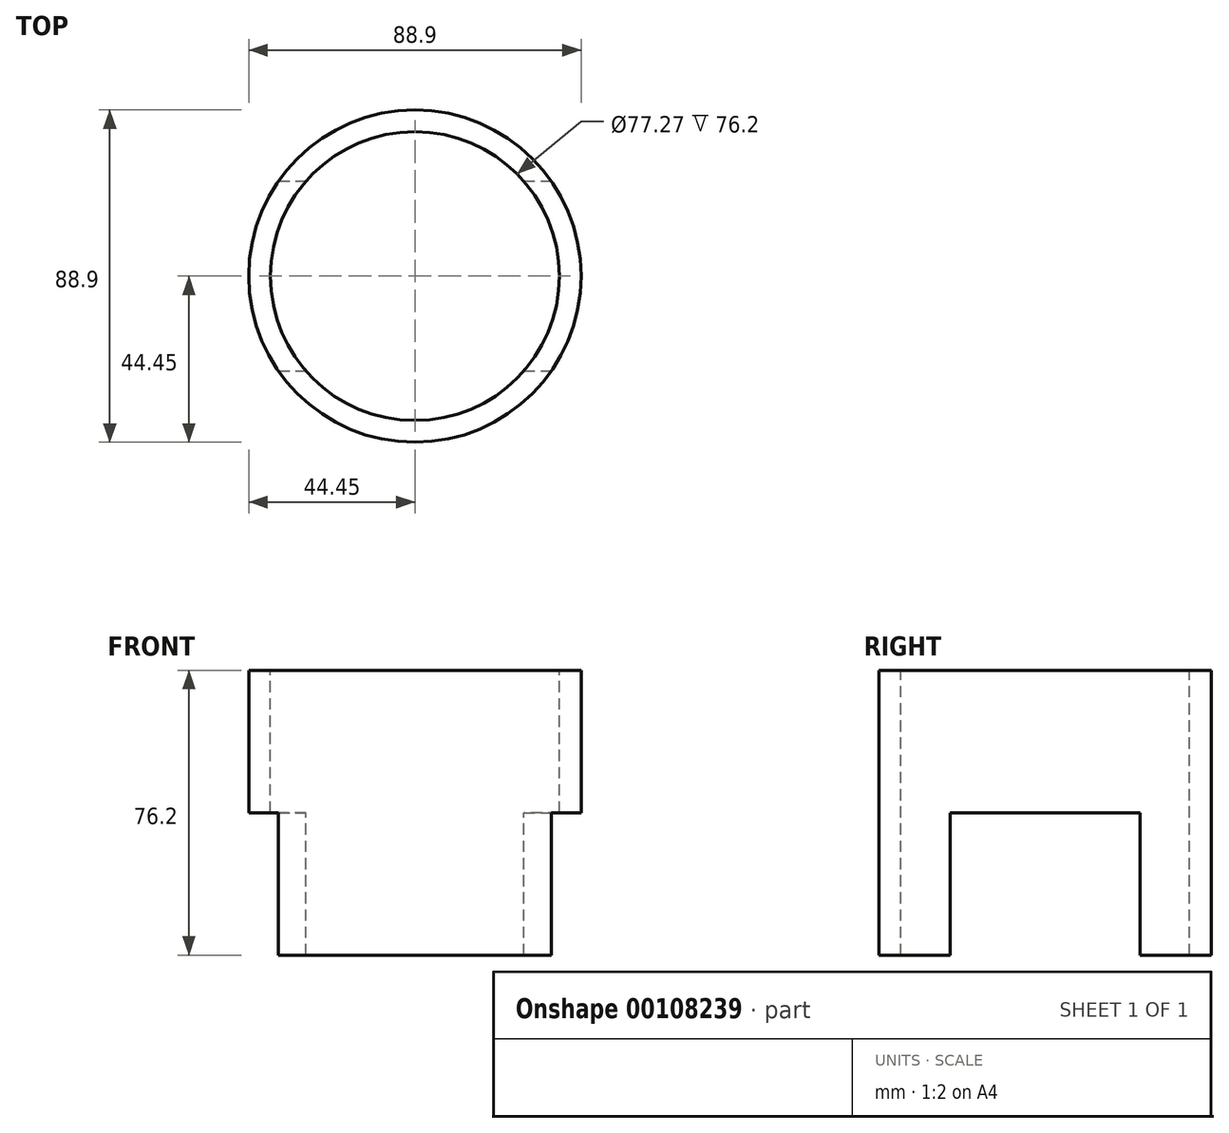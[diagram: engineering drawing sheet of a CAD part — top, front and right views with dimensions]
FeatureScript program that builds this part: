
annotation { "Feature Type Name" : "Feature", "Feature Type Description" : "" }
export const myFeature = defineFeature(function(context is Context, id is Id, definition is map)
    precondition{}
    {
        {
            var Q0;
            Q0=qCreatedBy(makeId("Front.planeOp"),FACE);
            var sketch = newSketch(context, id + "F0", { "sketchPlane" : qUnion([Q0])});
            skLineSegment(sketch, "E0", {"start": v(0, 190.5) * mm, "end": v(0, -190.5) * mm, "construction": true});
            skLineSegment(sketch, "E1", {"start": v(38.63, -38.1) * mm, "end": v(38.63, 38.1) * mm});
            skLineSegment(sketch, "E2", {"start": v(44.45, 38.1) * mm, "end": v(44.45, -38.1) * mm});
            skPoint(sketch, "E3", {"position": v(38.63, 0) * mm});
            skLineSegment(sketch, "E4", {"start": v(38.63, 38.1) * mm, "end": v(44.45, 38.1) * mm});
            skLineSegment(sketch, "E5", {"start": v(38.63, -38.1) * mm, "end": v(44.45, -38.1) * mm});
            skSolve(sketch);
        }
        {
            var Q0;
            Q0=makeQuery(id+"F0.imprint","IMPRINT",FACE,{"disambiguationData":[TD([[makeQuery(id+"F0.imprint","IMPRINT",EDGE,{"derivedFrom":sQuery(id+"F0.wireOp",EDGE,"E1")}),-1.0]])]});
            var Q1;
            Q1=sQuery(id+"F0.wireOp",EDGE,"E0");
            revolve(context, id + "F1", {"entities" : qUnion([Q0]), "axis" : qUnion([Q1]), "revolveType" : RevolveType.FULL});
        }
        {
            var Q0;
            Q0=qCreatedBy(makeId("Right.planeOp"),FACE);
            var sketch = newSketch(context, id + "F2", { "sketchPlane" : qUnion([Q0])});
            skLineSegment(sketch, "E6.bottom", {"start": v(25.4, 0) * mm, "end": v(-25.4, 0) * mm});
            skLineSegment(sketch, "E6.top", {"start": v(25.4, -38.1) * mm, "end": v(-25.4, -38.1) * mm});
            skLineSegment(sketch, "E6.left", {"start": v(25.4, 0) * mm, "end": v(25.4, -38.1) * mm});
            skLineSegment(sketch, "E6.right", {"start": v(-25.4, 0) * mm, "end": v(-25.4, -38.1) * mm});
            skPoint(sketch, "E7", {"position": v(0, 0) * mm});
            skSolve(sketch);
        }
        {
            var Q0;
            Q0 = qSketchRegion(id + "F2", true);
            extrude(context, id + "F3", {"entities" : qUnion([Q0]), "operationType" : NewBodyOperationType.REMOVE, "endBound" : BoundingType.SYMMETRIC, "oppositeDirection" : true, "depth" : 1066.8 * mm});
        }
    });
